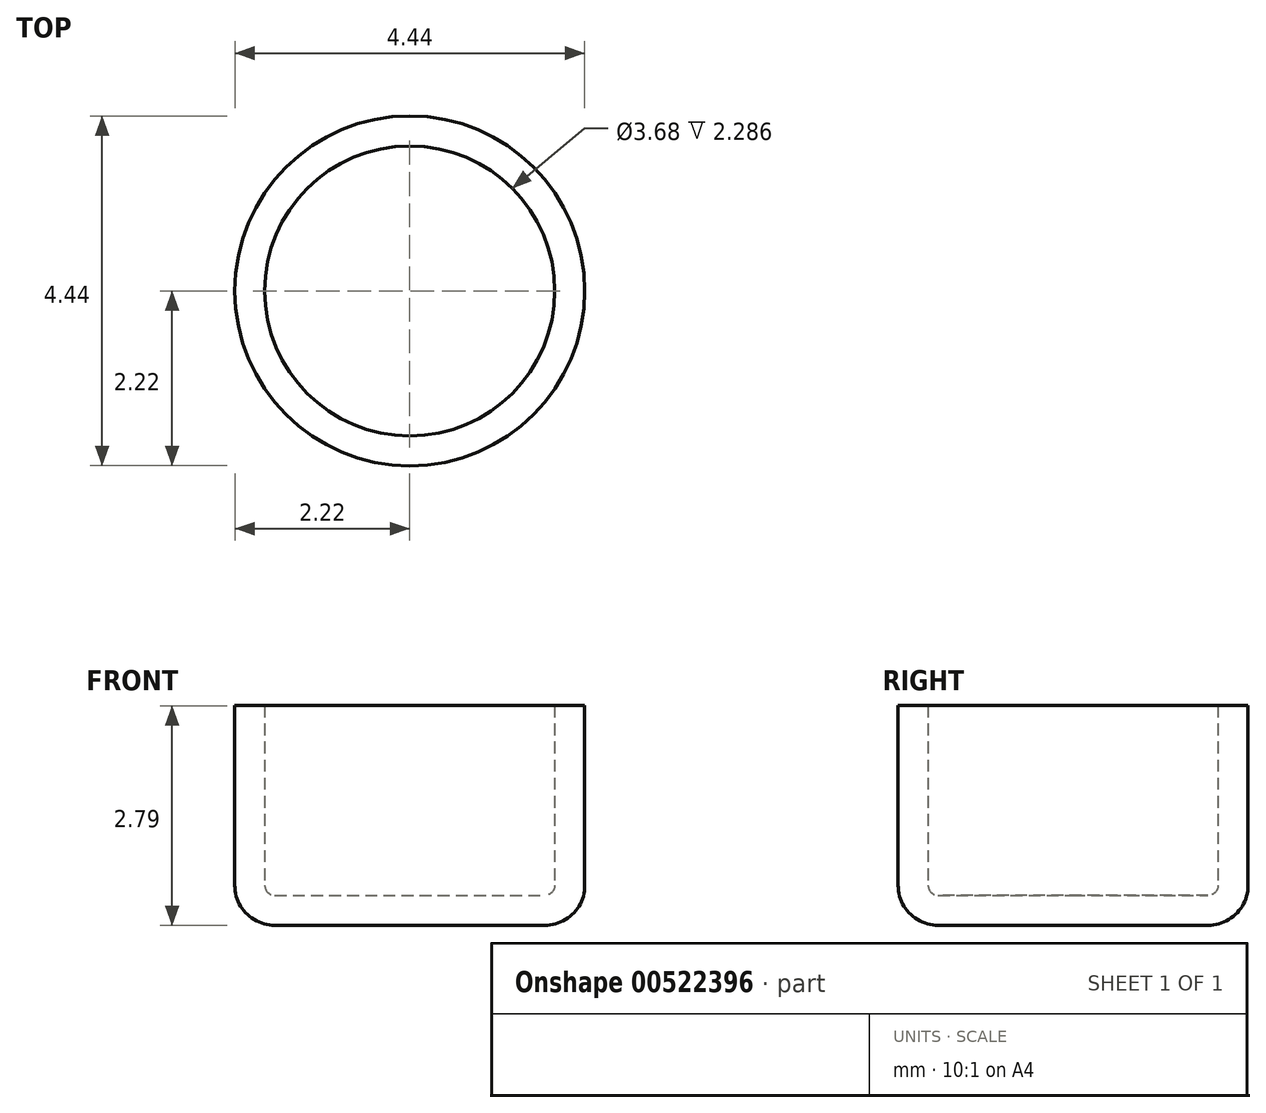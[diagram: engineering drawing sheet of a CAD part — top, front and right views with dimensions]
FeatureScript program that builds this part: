
annotation { "Feature Type Name" : "Feature", "Feature Type Description" : "" }
export const myFeature = defineFeature(function(context is Context, id is Id, definition is map)
    precondition{}
    {
        {
            var Q0;
            Q0=qCreatedBy(makeId("Front.planeOp"),FACE);
            var sketch = newSketch(context, id + "F0", { "sketchPlane" : qUnion([Q0])});
            skLineSegment(sketch, "E0", {"start": v(0, 0) * mm, "end": v(0, 0.38) * mm});
            skLineSegment(sketch, "E1", {"start": v(0, 0.38) * mm, "end": v(1.71, 0.38) * mm});
            skLineSegment(sketch, "E2", {"start": v(1.84, 0.5) * mm, "end": v(1.84, 2.8) * mm});
            skLineSegment(sketch, "E3", {"start": v(1.84, 2.8) * mm, "end": v(2.22, 2.8) * mm});
            skLineSegment(sketch, "E4", {"start": v(2.22, 2.8) * mm, "end": v(2.22, 0.5) * mm});
            skLineSegment(sketch, "E5", {"start": v(1.71, 0) * mm, "end": v(0, 0) * mm});
            skPoint(sketch, "E6.visualSharp", {"position": v(2.22, 0) * mm});
            skArc(sketch, "E6.filletArc", {"start": v(1.71, 0) * mm, "mid": v(2.07, 0.15) * mm, "end": v(2.22, 0.5) * mm});
            skPoint(sketch, "E7.visualSharp", {"position": v(1.84, 0.38) * mm});
            skArc(sketch, "E7.filletArc", {"start": v(1.71, 0.38) * mm, "mid": v(1.8, 0.42) * mm, "end": v(1.84, 0.5) * mm});
            skSolve(sketch);
        }
        {
            var Q0;
            Q0 = qSketchRegion(id + "F0", true);
            var Q1;
            Q1=sQuery(id+"F0.wireOp",EDGE,"E0");
            revolve(context, id + "F1", {"entities" : qUnion([Q0]), "axis" : qUnion([Q1]), "revolveType" : RevolveType.FULL});
        }
    });
